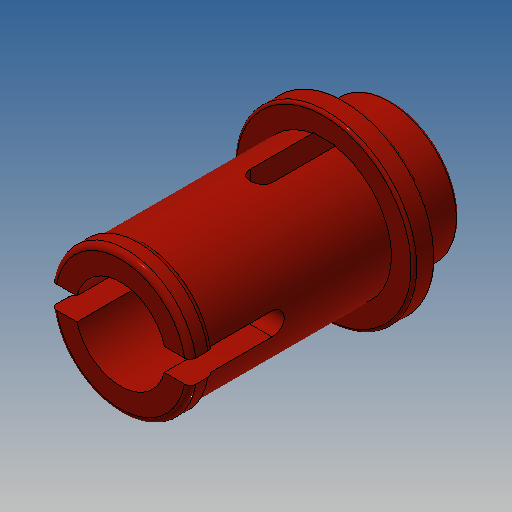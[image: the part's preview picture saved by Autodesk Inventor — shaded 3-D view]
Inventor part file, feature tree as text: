
AUTODESK INVENTOR PART (.ipt)
format: ipt  version: 2025 (Build 290162010, 162A)  size: 280,064 bytes
history: native  units: mm (DEFAULTED — no unit token found)
features: sketch x2, extrude x2, revolve x1, fillet x1
ambient origin geometry x8: Origin, YZ Plane, XZ Plane, XY Plane, X Axis, Y Axis, Z Axis, Center Point
bodies: Solid2 (feature_tree)
feature tree (6):
  sketch  "Sketch1"  dims[d1=4.8mm d2=5.0mm d6=8.0mm]
  revolve  "Revolution1"  [1 undecoded]
  fillet  "Fillet1"  Radius=8.0mm
  extrude  "Extrusion1"  Depth=0.8mm
  extrude  "Extrusion2"  Depth=0.8mm
  sketch  "Sketch2"  dims[d7=0.8mm d8=6.4mm d9=0.8mm d14=0.8mm d19=8.0mm d20=90.0deg d21=4.8mm d22=0.0mm d25=10.0mm d26=0.0mm d27=0.2mm d28=0.1mm d29=0.0mm d30=0.0mm d32=3.4mm d33=1.6mm d34=3.4mm d35=0.8mm d36=0.0mm d37=3.2mm d38=4.8mm]
note: 1 required parameter value undecoded (feature->parameter linkage not recoverable at this tier; creation-order binding heuristic only, values carry confidence <= 0.55)
